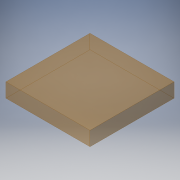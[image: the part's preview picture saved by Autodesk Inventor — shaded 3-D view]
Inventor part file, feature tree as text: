
AUTODESK INVENTOR PART (.ipt)
format: ipt  version: 2016 (Build 200138000, 138)  size: 104,448 bytes
history: native  units: in
note: dims shown in document units (in); Inventor stores cm internally (conversion verified against a paired STEP export)
features: extrude x1, sketch x1
ambient origin geometry x8: Origin, YZ Plane, XZ Plane, XY Plane, X Axis, Y Axis, Z Axis, Center Point
bodies: Solid1 (feature_tree)
feature tree (2):
  extrude  "Extrusion1"  Depth=11.811in
  sketch  "Sketch1"  dims[d0=11.811in d1=11.811in d2=2.0in d3=0.0in]
